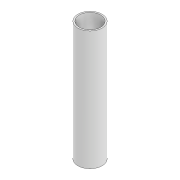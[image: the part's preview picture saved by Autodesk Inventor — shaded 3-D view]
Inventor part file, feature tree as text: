
AUTODESK INVENTOR PART (.ipt)
format: ipt  version: 2022.3 (Build 263350000, 350)  size: 99,328 bytes
history: native  units: mm
features: other x1, extrude x1, sketch x1
ambient origin geometry x8: Origin, YZ Plane, XZ Plane, XY Plane, X Axis, Y Axis, Z Axis, Center Point
bodies: Body1 (feature_tree)
feature tree (3):
  other  "Sólido1"
  extrude  "Extrusión1"  Depth=245.0mm
  sketch  "Boceto1"  dims[d0=49.75mm d1=43.9mm d2=245.0mm d3=0.0mm]
